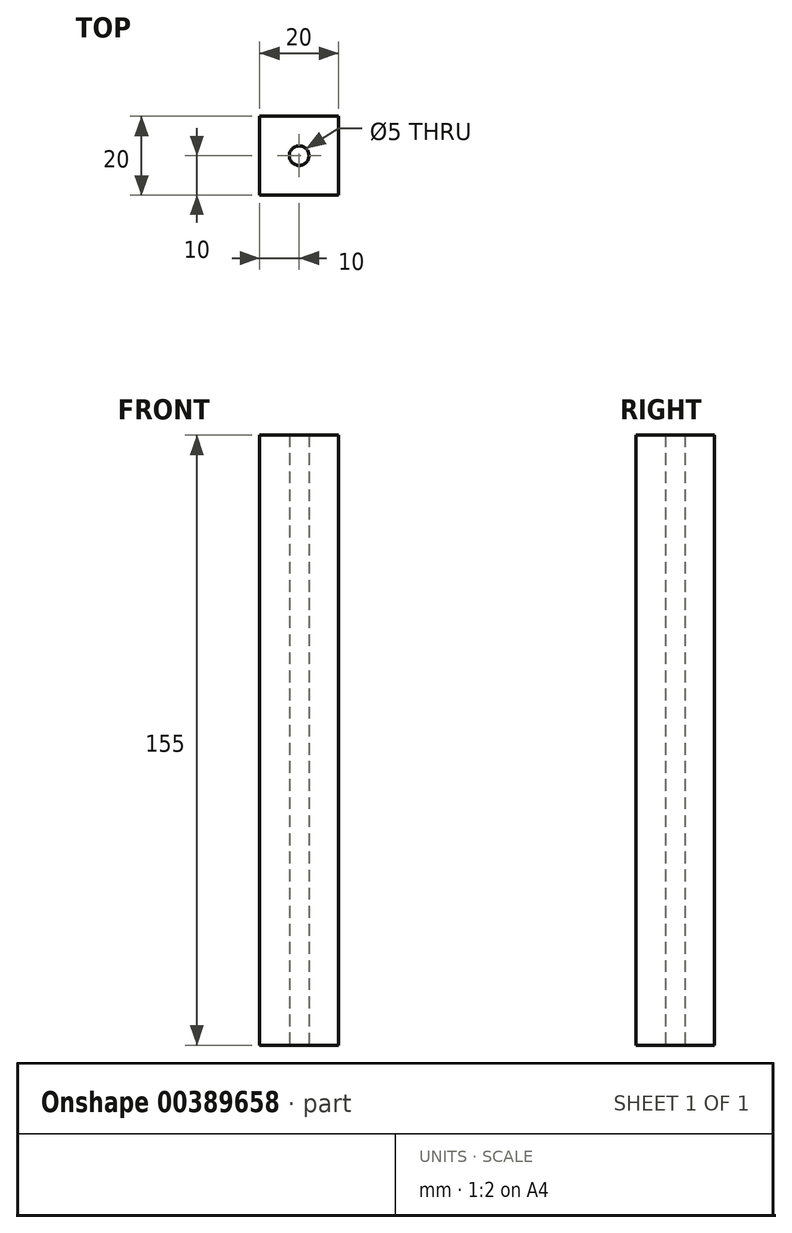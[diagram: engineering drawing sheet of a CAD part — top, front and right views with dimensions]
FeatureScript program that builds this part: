
annotation { "Feature Type Name" : "Feature", "Feature Type Description" : "" }
export const myFeature = defineFeature(function(context is Context, id is Id, definition is map)
    precondition{}
    {
        {
            var Q0;
            Q0=qCreatedBy(makeId("Top.planeOp"),FACE);
            var sketch = newSketch(context, id + "F0", { "sketchPlane" : qUnion([Q0])});
            skLineSegment(sketch, "E0.bottom", {"start": v(-10, 10) * mm, "end": v(10, 10) * mm});
            skLineSegment(sketch, "E0.top", {"start": v(-10, -10) * mm, "end": v(10, -10) * mm});
            skLineSegment(sketch, "E0.left", {"start": v(-10, 10) * mm, "end": v(-10, -10) * mm});
            skLineSegment(sketch, "E0.right", {"start": v(10, 10) * mm, "end": v(10, -10) * mm});
            skCircle(sketch, "E1", {"center": v(0, 0) * mm, "radius": 2.5 * mm});
            skSolve(sketch);
        }
        {
            var Q0;
            Q0=qSketchRegion(id+"F0",true);
            extrude(context, id + "F1", {"entities" : qUnion([Q0]), "depth" : 155 * mm});
        }
        {
            var Q0;
            Q0=makeQuery(id+"F1.opExtrude","SWEPT_FACE",FACE,{"disambiguationData":[OSD([sQuery(id+"F0.wireOp",EDGE,"E0.right")])]});
            var sketch = newSketch(context, id + "F2", { "sketchPlane" : qUnion([Q0])});
            skCircle(sketch, "E2", {"center": v(0, 10) * mm, "radius": 2.5 * mm});
            skSolve(sketch);
        }
    });
